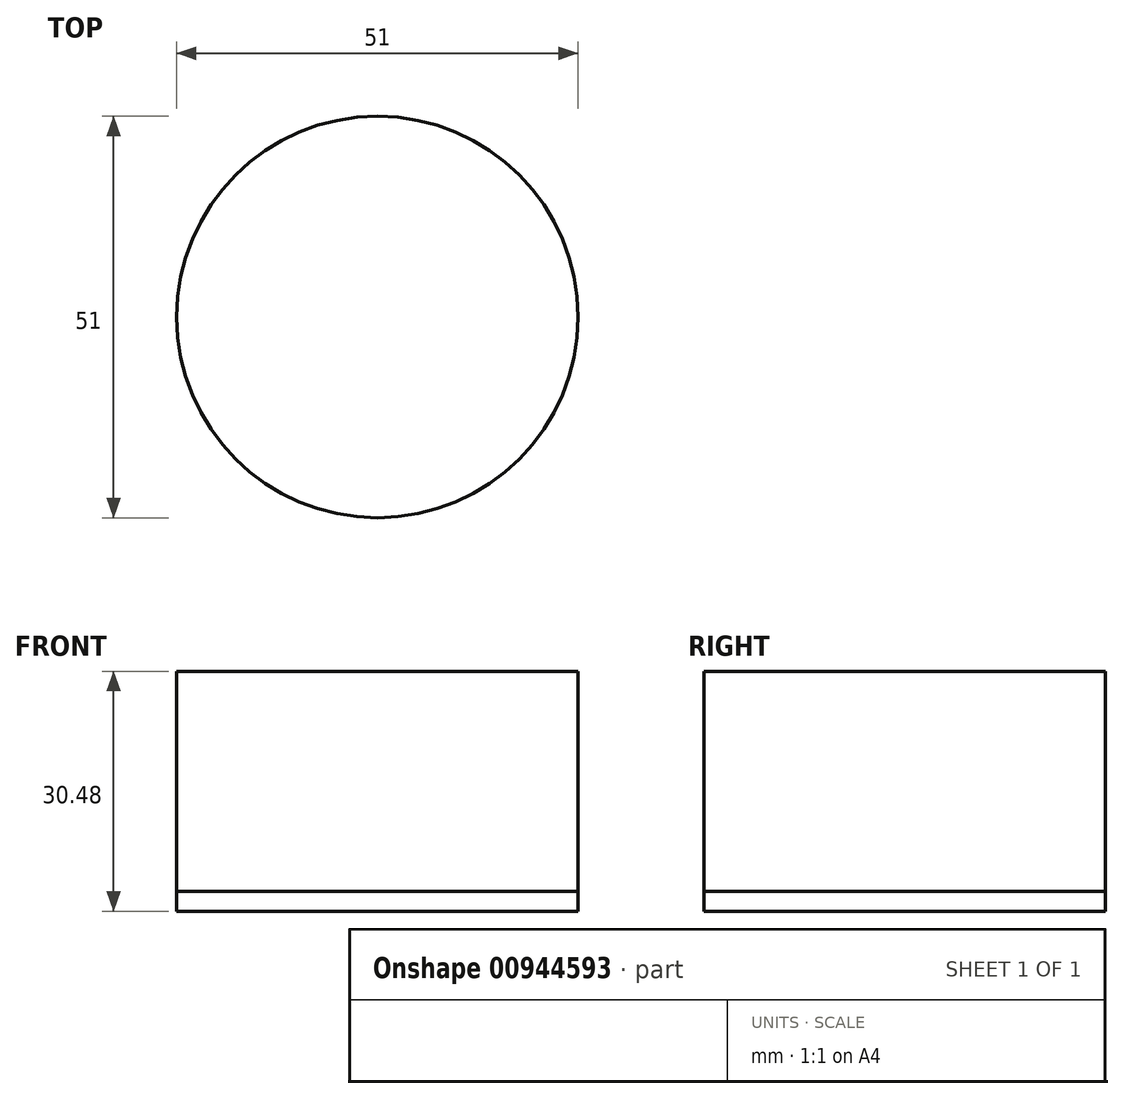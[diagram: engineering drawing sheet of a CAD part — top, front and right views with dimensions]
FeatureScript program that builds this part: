
annotation { "Feature Type Name" : "Feature", "Feature Type Description" : "" }
export const myFeature = defineFeature(function(context is Context, id is Id, definition is map)
    precondition{}
    {
        {
            var Q0;
            Q0=qCreatedBy(makeId("Top.planeOp"),FACE);
            var sketch = newSketch(context, id + "F0", { "sketchPlane" : qUnion([Q0])});
            skCircle(sketch, "E0", {"center": v(0, 0) * mm, "radius": 25.5 * mm});
            skSolve(sketch);
        }
        {
            var Q0;
            Q0 = qSketchRegion(id + "F0", true);
            extrude(context, id + "F1", {"entities" : qUnion([Q0]), "depth" : 25.4 * mm, "offsetDistance" : 25.4 * mm});
        }
        {
            var Q0;
            Q0=makeQuery(id+"F1.opExtrude","CAP_FACE",FACE,{"disambiguationData":[OSD([sQuery(id+"F0.wireOp",EDGE,"E0")])],"isStart":true});
            extrude(context, id + "F2", {"entities" : qUnion([Q0]), "depth" : 2.54 * mm, "offsetDistance" : 25.4 * mm});
        }
        {
            var Q0;
            Q0=makeQuery(id+"F1.opExtrude","CAP_FACE",FACE,{"disambiguationData":[OSD([sQuery(id+"F0.wireOp",EDGE,"E0")])],"isStart":false});
            extrude(context, id + "F3", {"entities" : qUnion([Q0]), "operationType" : NewBodyOperationType.ADD, "depth" : 2.54 * mm, "offsetDistance" : 25.4 * mm});
        }
    });
